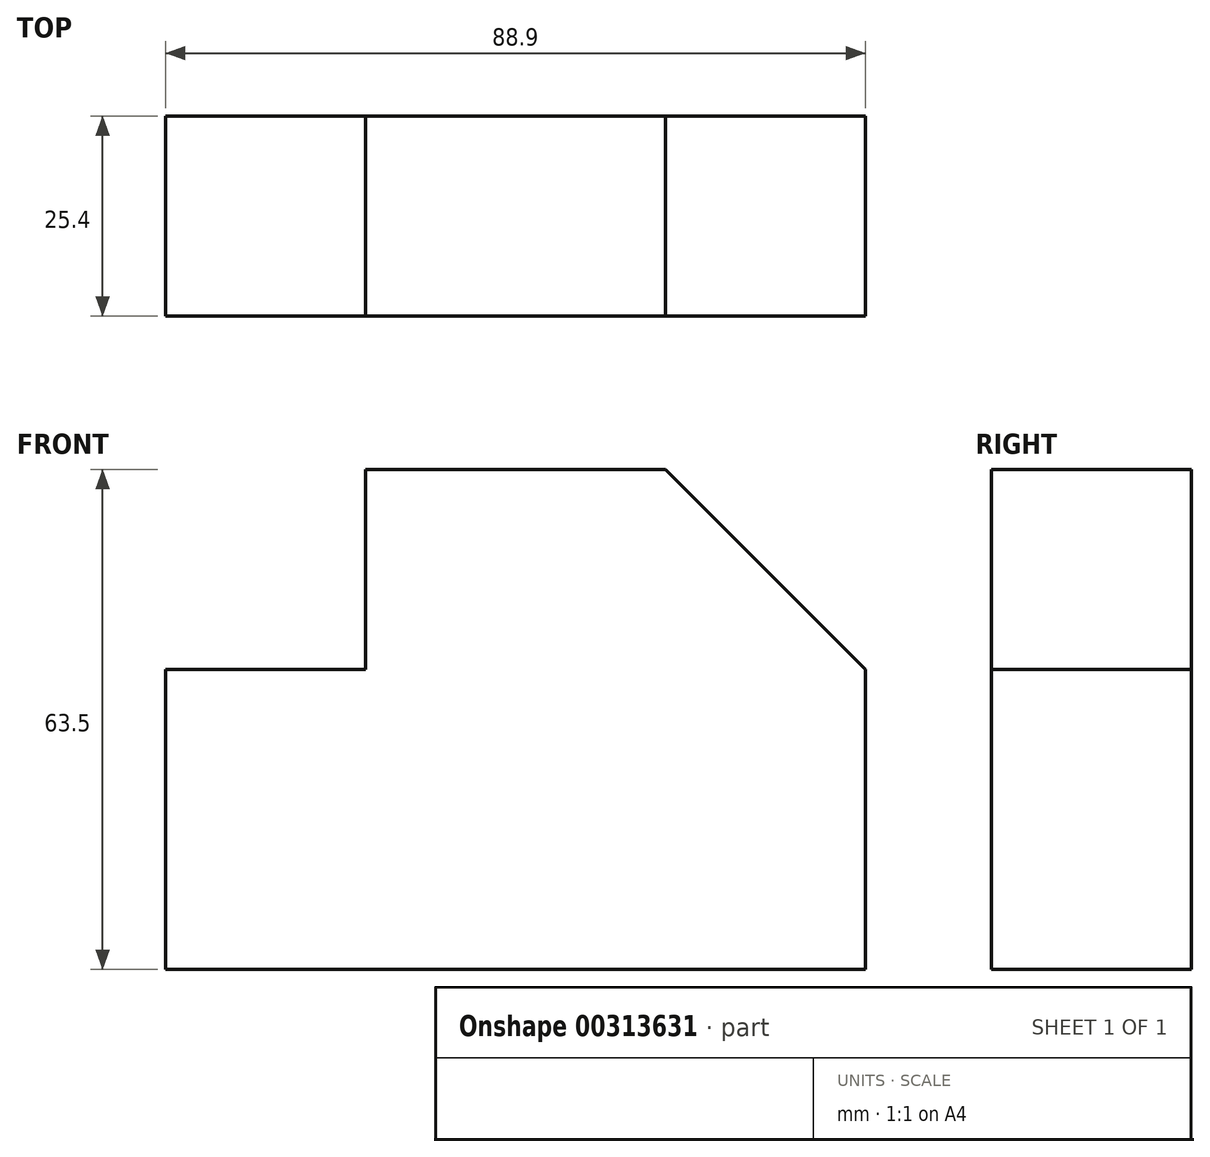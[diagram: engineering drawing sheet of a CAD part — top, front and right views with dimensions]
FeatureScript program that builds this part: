
annotation { "Feature Type Name" : "Feature", "Feature Type Description" : "" }
export const myFeature = defineFeature(function(context is Context, id is Id, definition is map)
    precondition{}
    {
        {
            var Q0;
            Q0=qCreatedBy(makeId("Front.planeOp"),FACE);
            var sketch = newSketch(context, id + "F0", { "sketchPlane" : qUnion([Q0])});
            skLineSegment(sketch, "E0", {"start": v(-46.15, -38.52) * mm, "end": v(42.75, -38.52) * mm});
            skLineSegment(sketch, "E1", {"start": v(-46.15, -38.52) * mm, "end": v(-46.15, -0.42) * mm});
            skLineSegment(sketch, "E2", {"start": v(-46.15, -0.42) * mm, "end": v(-20.75, -0.42) * mm});
            skLineSegment(sketch, "E3", {"start": v(-20.75, -0.42) * mm, "end": v(-20.75, 24.98) * mm});
            skLineSegment(sketch, "E4", {"start": v(-20.75, 24.98) * mm, "end": v(17.35, 24.98) * mm});
            skLineSegment(sketch, "E5", {"start": v(17.35, 24.98) * mm, "end": v(42.75, -0.42) * mm});
            skLineSegment(sketch, "E6", {"start": v(42.75, -0.42) * mm, "end": v(42.75, -38.52) * mm});
            skSolve(sketch);
        }
        {
            var Q0;
            Q0=makeQuery(id+"F0.imprint","IMPRINT",FACE,{"disambiguationData":[TD([[makeQuery(id+"F0.imprint","IMPRINT",EDGE,{"derivedFrom":sQuery(id+"F0.wireOp",EDGE,"E0")}),1.0]])]});
            extrude(context, id + "F1", {"entities" : qUnion([Q0]), "depth" : 25.4 * mm});
        }
    });
